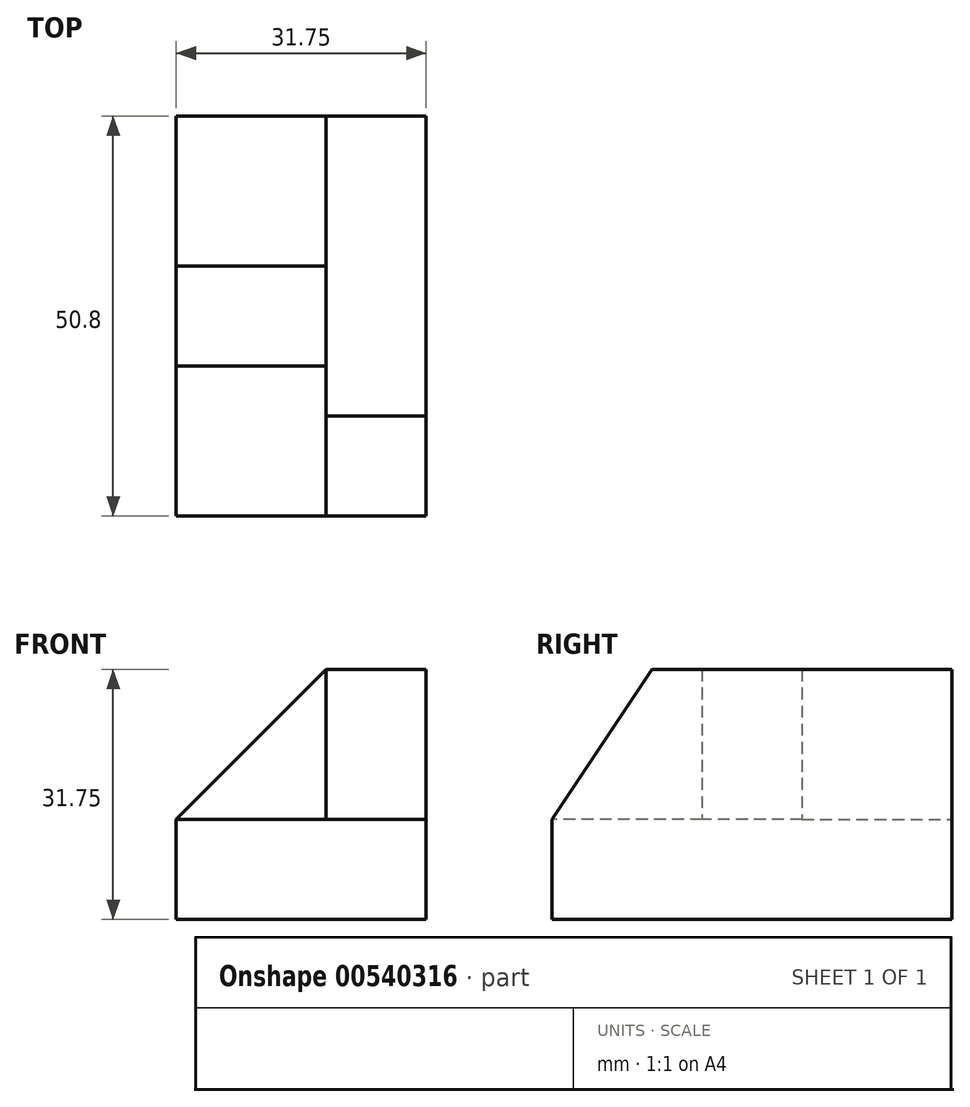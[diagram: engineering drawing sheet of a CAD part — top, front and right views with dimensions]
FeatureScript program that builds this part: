
annotation { "Feature Type Name" : "Feature", "Feature Type Description" : "" }
export const myFeature = defineFeature(function(context is Context, id is Id, definition is map)
    precondition{}
    {
        {
            var Q0;
            Q0=qCreatedBy(makeId("Right.planeOp"),FACE);
            var sketch = newSketch(context, id + "F0", { "sketchPlane" : qUnion([Q0])});
            skLineSegment(sketch, "E0.bottom", {"start": v(-50.8, 31.75) * mm, "end": v(0, 31.75) * mm});
            skLineSegment(sketch, "E0.top", {"start": v(-50.8, 0) * mm, "end": v(0, 0) * mm});
            skLineSegment(sketch, "E0.left", {"start": v(-50.8, 31.75) * mm, "end": v(-50.8, 0) * mm});
            skLineSegment(sketch, "E0.right", {"start": v(0, 31.75) * mm, "end": v(0, 0) * mm});
            skSolve(sketch);
        }
        {
            var Q0;
            Q0=makeQuery(id+"F0.imprint","IMPRINT",FACE,{"disambiguationData":[TD([[makeQuery(id+"F0.imprint","IMPRINT",EDGE,{"derivedFrom":sQuery(id+"F0.wireOp",EDGE,"E0.bottom")}),-1.0]])]});
            extrude(context, id + "F1", {"entities" : qUnion([Q0]), "depth" : 31.75 * mm, "offsetDistance" : 25.4 * mm});
        }
        {
            var Q0;
            Q0=makeQuery(id+"F1.opExtrude","SWEPT_FACE",FACE,{"disambiguationData":[OSD([sQuery(id+"F0.wireOp",EDGE,"E0.right")])]});
            var sketch = newSketch(context, id + "F2", { "sketchPlane" : qUnion([Q0])});
            skLineSegment(sketch, "E1", {"start": v(-19.05, 31.75) * mm, "end": v(-19.05, 12.7) * mm});
            skLineSegment(sketch, "E2", {"start": v(-19.05, 12.7) * mm, "end": v(0, 12.7) * mm});
            skSolve(sketch);
        }
        {
            var Q0;
            Q0 = qSketchRegion(id + "F2", true);
            var Q1;
            {var subQ0=sQuery(id+"F2.wireOp",EDGE,"E1");Q1=makeQuery(id+"F2.imprint","IMPRINT",FACE,{"disambiguationData":[TD([[makeQuery(id+"F2.imprint","IMPRINT",EDGE,{"derivedFrom":subQ0}),1.0]])]});}
            extrude(context, id + "F3", {"entities" : qUnion([Q0, Q1]), "operationType" : NewBodyOperationType.REMOVE, "oppositeDirection" : true, "depth" : 19.05 * mm, "offsetDistance" : 25.4 * mm});
        }
        {
            var Q0;
            Q0=makeQuery(id+"F1.opExtrude","SWEPT_FACE",FACE,{"disambiguationData":[OSD([sQuery(id+"F0.wireOp",EDGE,"E0.left")])]});
            var sketch = newSketch(context, id + "F4", { "sketchPlane" : qUnion([Q0])});
            skLineSegment(sketch, "E3", {"start": v(19.05, 31.75) * mm, "end": v(19.05, 12.7) * mm});
            skLineSegment(sketch, "E4", {"start": v(19.05, 12.7) * mm, "end": v(0, 12.7) * mm});
            skSolve(sketch);
        }
        {
            var Q0;
            Q0 = qSketchRegion(id + "F4", true);
            var Q1;
            {var subQ0=sQuery(id+"F4.wireOp",EDGE,"E3");Q1=makeQuery(id+"F4.imprint","IMPRINT",FACE,{"disambiguationData":[TD([[makeQuery(id+"F4.imprint","IMPRINT",EDGE,{"derivedFrom":subQ0}),-1.0]])]});}
            extrude(context, id + "F5", {"entities" : qUnion([Q0, Q1]), "operationType" : NewBodyOperationType.REMOVE, "oppositeDirection" : true, "depth" : 19.05 * mm, "offsetDistance" : 25.4 * mm});
        }
        {
            var Q0;
            Q0=makeQuery(id+"F5.boolean.opBoolean","COPY",FACE,{"derivedFrom":makeQuery(id+"F5.opExtrude","SWEPT_FACE",FACE,{"disambiguationData":[OSD([sQuery(id+"F4.wireOp",EDGE,"E3")])]})});
            var sketch = newSketch(context, id + "F6", { "sketchPlane" : qUnion([Q0])});
            skLineSegment(sketch, "E5", {"start": v(31.75, 31.75) * mm, "end": v(38.1, 31.75) * mm});
            skLineSegment(sketch, "E6", {"start": v(50.8, 12.7) * mm, "end": v(38.1, 31.75) * mm});
            skSolve(sketch);
        }
        {
            var Q0;
            Q0 = qSketchRegion(id + "F6", true);
            var Q1;
            {var subQ0=sQuery(id+"F6.wireOp",EDGE,"E6");Q1=makeQuery(id+"F6.imprint","IMPRINT",FACE,{"disambiguationData":[TD([[makeQuery(id+"F6.imprint","IMPRINT",EDGE,{"derivedFrom":subQ0}),-1.0]])]});}
            extrude(context, id + "F7", {"entities" : qUnion([Q0, Q1]), "operationType" : NewBodyOperationType.REMOVE, "oppositeDirection" : true, "depth" : 25.4 * mm, "offsetDistance" : 25.4 * mm});
        }
        {
            var Q0;
            Q0=makeQuery(id+"F5.boolean.opBoolean","COPY",FACE,{"derivedFrom":makeQuery(id+"F5.opExtrude","CAP_FACE",FACE,{"disambiguationData":[OSD([sQuery(id+"F0.wireOp",EDGE,"E0.bottom"),sQuery(id+"F0.wireOp",EDGE,"E0.left"),sQuery(id+"F4.wireOp",EDGE,"E3"),sQuery(id+"F4.wireOp",EDGE,"E4")])],"isStart":false})});
            var sketch = newSketch(context, id + "F8", { "sketchPlane" : qUnion([Q0])});
            skLineSegment(sketch, "E7", {"start": v(0, 12.7) * mm, "end": v(19.05, 31.75) * mm});
            skSolve(sketch);
        }
        {
            var Q0;
            Q0 = qSketchRegion(id + "F8", true);
            var Q1;
            Q1=makeQuery(id+"F8.imprint","IMPRINT",FACE,{"disambiguationData":[TD([[makeQuery(id+"F8.imprint","IMPRINT",EDGE,{"derivedFrom":sQuery(id+"F8.wireOp",EDGE,"E7")}),1.0]])]});
            extrude(context, id + "F9", {"entities" : qUnion([Q0, Q1]), "operationType" : NewBodyOperationType.REMOVE, "oppositeDirection" : true, "depth" : 25.4 * mm, "offsetDistance" : 25.4 * mm});
        }
    });
